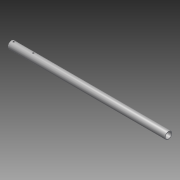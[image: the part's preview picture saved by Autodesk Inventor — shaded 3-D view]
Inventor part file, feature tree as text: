
AUTODESK INVENTOR PART (.ipt)
format: ipt  version: 2014 (Build 180170000, 170)  size: 123,392 bytes
history: native  units: in
note: dims shown in document units (in); Inventor stores cm internally (conversion verified against a paired STEP export)
features: other x2, extrude x2, sketch x2, plane x1, imported_body x1, projected_geometry x1
ambient origin geometry x8: Origin, YZ Plane, XZ Plane, XY Plane, X Axis, Y Axis, Z Axis, Center Point
bodies: Body1 (feature_tree)
feature tree (9):
  parser-record x1  (decoder bookkeeping rows leaked as tree rows — omitted from the tree; the rows remain in map.json)
  other  "4347K3111"
  extrude  "Extrusion1"  Depth=0.19in
  plane  "Work Plane1"
  extrude  "Extrusion2"  Depth=2.5in
  imported_body  "Base1"
  sketch  "Sketch1"  dims[d0=6.0in d1=0.0in d2=0.19in]
  sketch  "Sketch2"  dims[d3=0.25in d4=2.5in d5=1.0in d6=0.0in]
  projected_geometry  "Projected Loop1"
